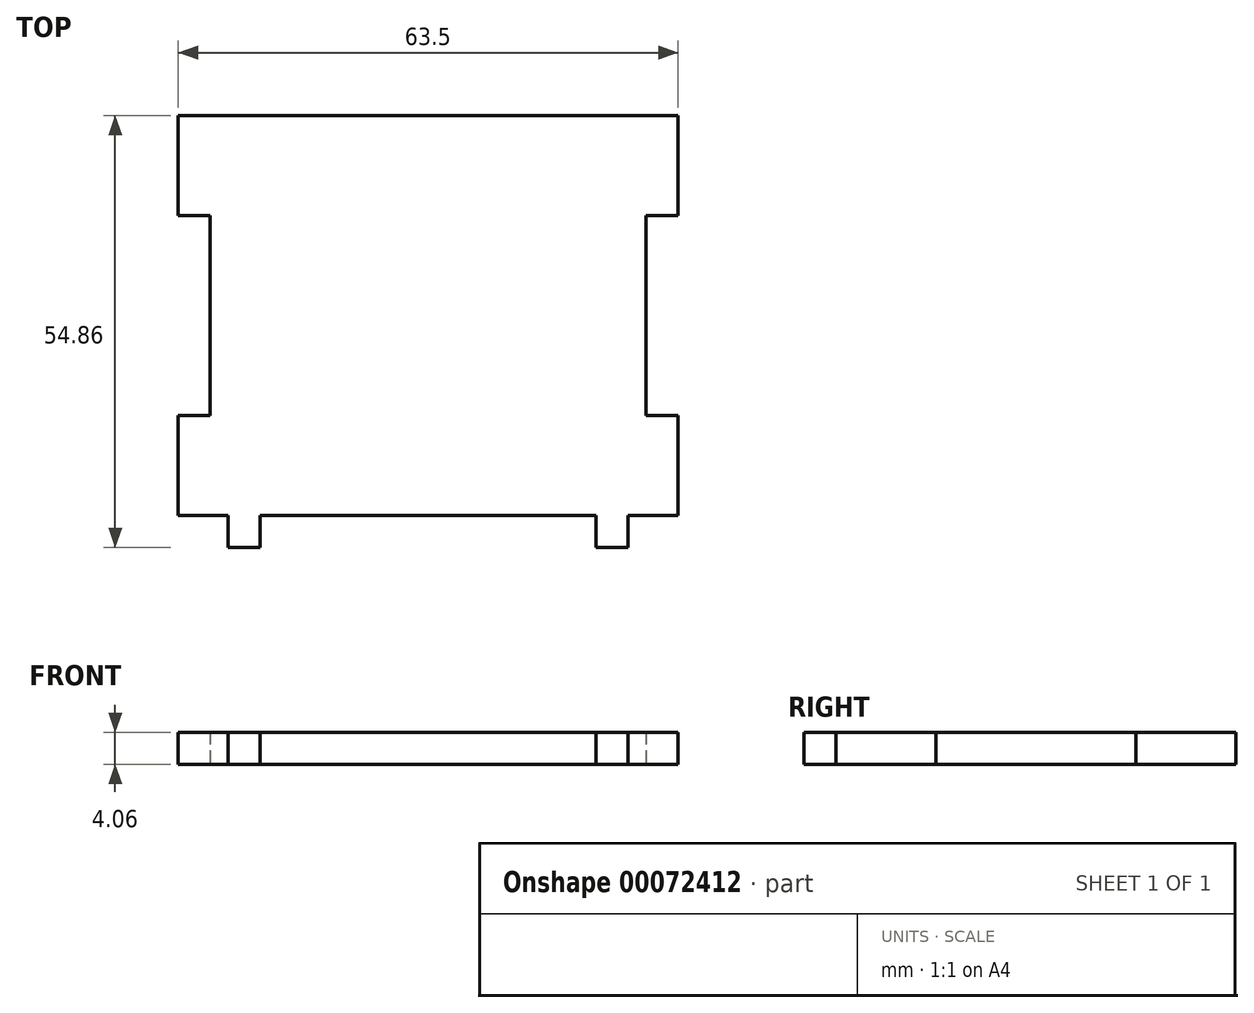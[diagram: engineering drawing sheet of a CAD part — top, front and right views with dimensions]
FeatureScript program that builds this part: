
annotation { "Feature Type Name" : "Feature", "Feature Type Description" : "" }
export const myFeature = defineFeature(function(context is Context, id is Id, definition is map)
    precondition{}
    {
        {
            var Q0;
            Q0=qCreatedBy(makeId("Top.planeOp"),FACE);
            var sketch = newSketch(context, id + "F0", { "sketchPlane" : qUnion([Q0])});
            skLineSegment(sketch, "E0.rect.bottom", {"start": v(31.75, 25.4) * mm, "end": v(-31.75, 25.4) * mm});
            skLineSegment(sketch, "E0.rect.top", {"start": v(31.75, -25.4) * mm, "end": v(-31.75, -25.4) * mm});
            skLineSegment(sketch, "E0.rect.left", {"start": v(31.75, 25.4) * mm, "end": v(31.75, -25.4) * mm});
            skLineSegment(sketch, "E0.rect.right", {"start": v(-31.75, 25.4) * mm, "end": v(-31.75, -25.4) * mm});
            skPoint(sketch, "E0.rect.middle", {"position": v(0, 0) * mm});
            skLineSegment(sketch, "E1", {"start": v(0, 31.66) * mm, "end": v(0, -38.93) * mm, "construction": true});
            skLineSegment(sketch, "E2", {"start": v(-30.78, 0) * mm, "end": v(35.79, 0) * mm, "construction": true});
            skLineSegment(sketch, "E3.rect.bottom", {"start": v(27.69, 12.7) * mm, "end": v(31.75, 12.7) * mm});
            skLineSegment(sketch, "E3.rect.top", {"start": v(27.69, -12.7) * mm, "end": v(31.75, -12.7) * mm});
            skLineSegment(sketch, "E3.rect.left", {"start": v(27.69, 12.7) * mm, "end": v(27.69, -12.7) * mm});
            skLineSegment(sketch, "E3.rect.right", {"start": v(31.75, 12.7) * mm, "end": v(31.75, -12.7) * mm});
            skPoint(sketch, "E3.rect.middle", {"position": v(29.72, 0) * mm});
            skLineSegment(sketch, "E4.MirrorCS", {"start": v(-27.69, 12.7) * mm, "end": v(-27.69, -12.7) * mm});
            skLineSegment(sketch, "E5.MirrorCS", {"start": v(-27.69, 12.7) * mm, "end": v(-31.75, 12.7) * mm});
            skLineSegment(sketch, "E6.MirrorCS", {"start": v(-31.75, 12.7) * mm, "end": v(-31.75, -12.7) * mm});
            skLineSegment(sketch, "E7.MirrorCS", {"start": v(-27.69, -12.7) * mm, "end": v(-31.75, -12.7) * mm});
            skLineSegment(sketch, "E8.rect.bottom", {"start": v(25.4, -21.34) * mm, "end": v(-25.4, -21.34) * mm});
            skLineSegment(sketch, "E8.rect.top", {"start": v(25.4, -29.46) * mm, "end": v(-25.4, -29.46) * mm});
            skLineSegment(sketch, "E8.rect.left", {"start": v(25.4, -21.34) * mm, "end": v(25.4, -29.46) * mm});
            skLineSegment(sketch, "E8.rect.right", {"start": v(-25.4, -21.34) * mm, "end": v(-25.4, -29.46) * mm});
            skPoint(sketch, "E8.rect.middle", {"position": v(0, -25.4) * mm});
            skLineSegment(sketch, "E9", {"start": v(-21.34, -25.4) * mm, "end": v(-21.34, -29.46) * mm});
            skLineSegment(sketch, "E10.MirrorCS", {"start": v(-25.4, -29.46) * mm, "end": v(25.4, -29.46) * mm});
            skLineSegment(sketch, "E11.MirrorCS", {"start": v(21.34, -25.4) * mm, "end": v(21.34, -29.46) * mm});
            skSolve(sketch);
        }
        {
            var Q0;
            Q0=makeQuery(id+"F0.imprint","IMPRINT",FACE,{"disambiguationData":[TD([[makeQuery(id+"F0.imprint","IMPRINT",EDGE,{"derivedFrom":sQuery(id+"F0.wireOp",EDGE,"85baae9a-4184-45dd-bc90-eaca79e69f82.bottom")}),-1.0]])]});
            var Q1;
            Q1=makeQuery(id+"F0.imprint","IMPRINT",FACE,{"disambiguationData":[TD([[makeQuery(id+"F0.imprint","IMPRINT",EDGE,{"derivedFrom":sQuery(id+"F0.wireOp",EDGE,"e5e37f40-f2fa-44a4-80bb-a7cc98e88c2a0.MirrorCS")}),-1.0]])]});
            var Q2;
            Q2=makeQuery(id+"F0.imprint","IMPRINT",FACE,{"disambiguationData":[TD([[makeQuery(id+"F0.imprint","IMPRINT",EDGE,{"derivedFrom":sQuery(id+"F0.wireOp",EDGE,"E0.rect.bottom")}),1.0]])]});
            extrude(context, id + "F1", {"entities" : qUnion([Q0, Q1, Q2]), "depth" : 4.06 * mm});
        }
        {
            var Q0;
            {var subQ4=sQuery(id+"F0.wireOp",EDGE,"E8.rect.bottom");Q0=makeQuery(id+"F0.imprint","IMPRINT",FACE,{"disambiguationData":[TD([[makeQuery(id+"F0.imprint","IMPRINT",EDGE,{"derivedFrom":subQ4}),1.0]])]});}
            var Q1;
            {var subQ0=sQuery(id+"F0.wireOp",EDGE,"E11.MirrorCS");Q1=makeQuery(id+"F0.imprint","IMPRINT",FACE,{"disambiguationData":[TD([[makeQuery(id+"F0.imprint","IMPRINT",EDGE,{"derivedFrom":subQ0}),1.0]])]});}
            var Q2;
            {var subQ0=sQuery(id+"F0.wireOp",EDGE,"E9");Q2=makeQuery(id+"F0.imprint","IMPRINT",FACE,{"disambiguationData":[TD([[makeQuery(id+"F0.imprint","IMPRINT",EDGE,{"derivedFrom":subQ0}),-1.0]])]});}
            var Q3;
            Q3=makeQuery(id+"F0.imprint","IMPRINT",FACE,{"disambiguationData":[TD([[makeQuery(id+"F0.imprint","IMPRINT",EDGE,{"derivedFrom":sQuery(id+"F0.wireOp",EDGE,"E0.rect.bottom")}),1.0]])]});
            extrude(context, id + "F2", {"entities" : qUnion([Q0, Q1, Q2, Q3]), "operationType" : NewBodyOperationType.ADD, "depth" : 4.06 * mm});
        }
    });
